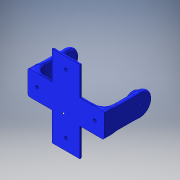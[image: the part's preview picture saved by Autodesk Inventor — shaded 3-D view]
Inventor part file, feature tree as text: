
AUTODESK INVENTOR PART (.ipt)
format: ipt  version: 2016 (Build 200138000, 138)  size: 442,880 bytes
history: native  units: in
note: dims shown in document units (in); Inventor stores cm internally (conversion verified against a paired STEP export)
features: sketch x11, other x3
ambient origin geometry x8: Origin, YZ Plane, XZ Plane, XY Plane, X Axis, Y Axis, Z Axis, Center Point
bodies: Solid1 (feature_tree)
feature tree (14):
  other  "Hip_forward.ipt"
  other  "Solid1::Hip_forward.ipt"
  other  "TaggingFeature1"
  sketch  "Sketch1"  dims[d0=0.3937in]
  sketch  "Sketch4"
  sketch  "Sketch5"
  sketch  "Sketch7"
  sketch  "Sketch9"
  sketch  "Sketch10"
  sketch  "Sketch15"
  sketch  "Sketch16"
  sketch  "Sketch17"
  sketch  "Sketch18"
  sketch  "Sketch19"
